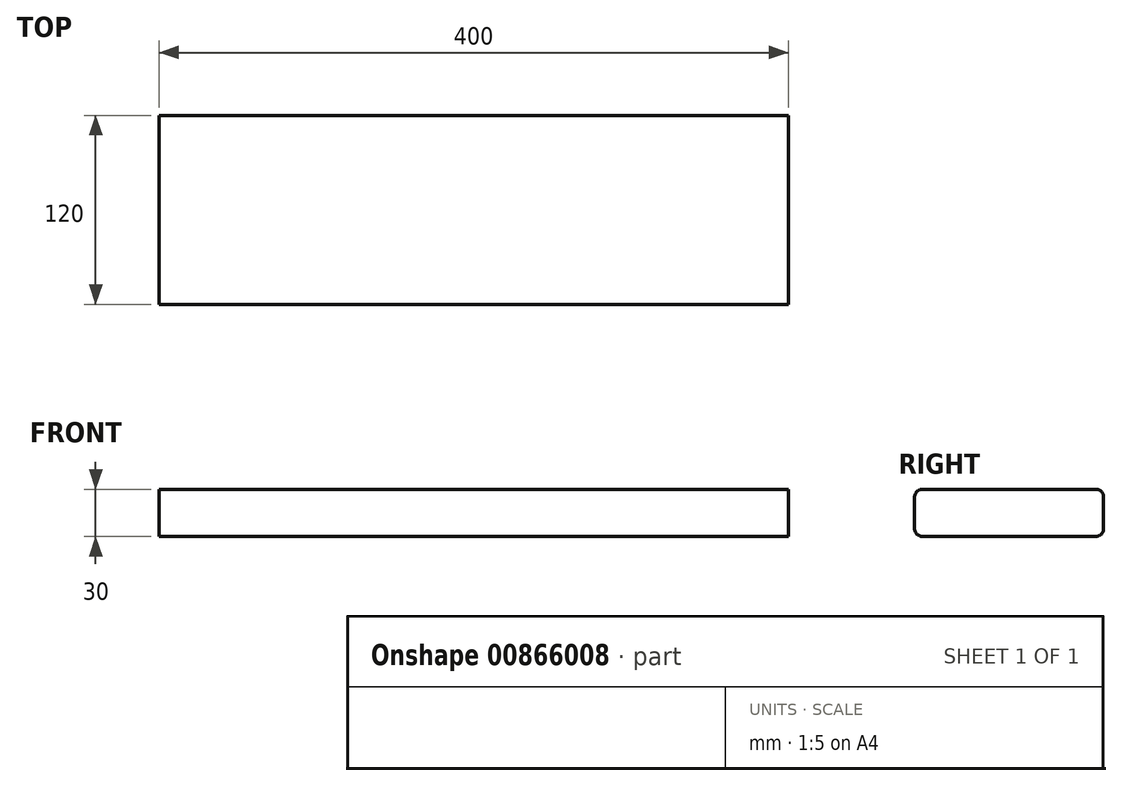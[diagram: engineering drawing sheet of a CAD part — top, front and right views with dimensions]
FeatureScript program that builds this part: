
annotation { "Feature Type Name" : "Feature", "Feature Type Description" : "" }
export const myFeature = defineFeature(function(context is Context, id is Id, definition is map)
    precondition{}
    {
        {
            var Q0;
            Q0=qCreatedBy(makeId("Front.planeOp"),FACE);
            var sketch = newSketch(context, id + "F0", { "sketchPlane" : qUnion([Q0])});
            skLineSegment(sketch, "E0.bottom", {"start": v(0, 0) * mm, "end": v(-400, 0) * mm});
            skLineSegment(sketch, "E0.top", {"start": v(0, -30) * mm, "end": v(-400, -30) * mm});
            skLineSegment(sketch, "E0.left", {"start": v(0, 0) * mm, "end": v(0, -30) * mm});
            skLineSegment(sketch, "E0.right", {"start": v(-400, 0) * mm, "end": v(-400, -30) * mm});
            skSolve(sketch);
        }
        {
            var Q0;
            Q0 = qSketchRegion(id + "F0", true);
            extrude(context, id + "F1", {"entities" : qUnion([Q0]), "depth" : 120 * mm, "offsetDistance" : 25 * mm});
        }
        {
            var Q0;
            Q0=makeQuery(id+"F1.opExtrude","CAP_EDGE",EDGE,{"disambiguationData":[OSD([sQuery(id+"F0.wireOp",EDGE,"E0.bottom")])],"isStart":false});
            var Q1;
            Q1=makeQuery(id+"F1.opExtrude","CAP_EDGE",EDGE,{"disambiguationData":[OSD([sQuery(id+"F0.wireOp",EDGE,"E0.top")])],"isStart":false});
            var Q2;
            Q2=makeQuery(id+"F1.opExtrude","CAP_EDGE",EDGE,{"disambiguationData":[OSD([sQuery(id+"F0.wireOp",EDGE,"E0.bottom")])],"isStart":true});
            var Q3;
            Q3=makeQuery(id+"F1.opExtrude","CAP_EDGE",EDGE,{"disambiguationData":[OSD([sQuery(id+"F0.wireOp",EDGE,"E0.top")])],"isStart":true});
            fillet(context, id + "F2", {"entities" : qUnion([Q0, Q1, Q2, Q3]), "radius" : 5 * mm, "tangentPropagation" : true, "allowEdgeOverflow" : false});
        }
    });
